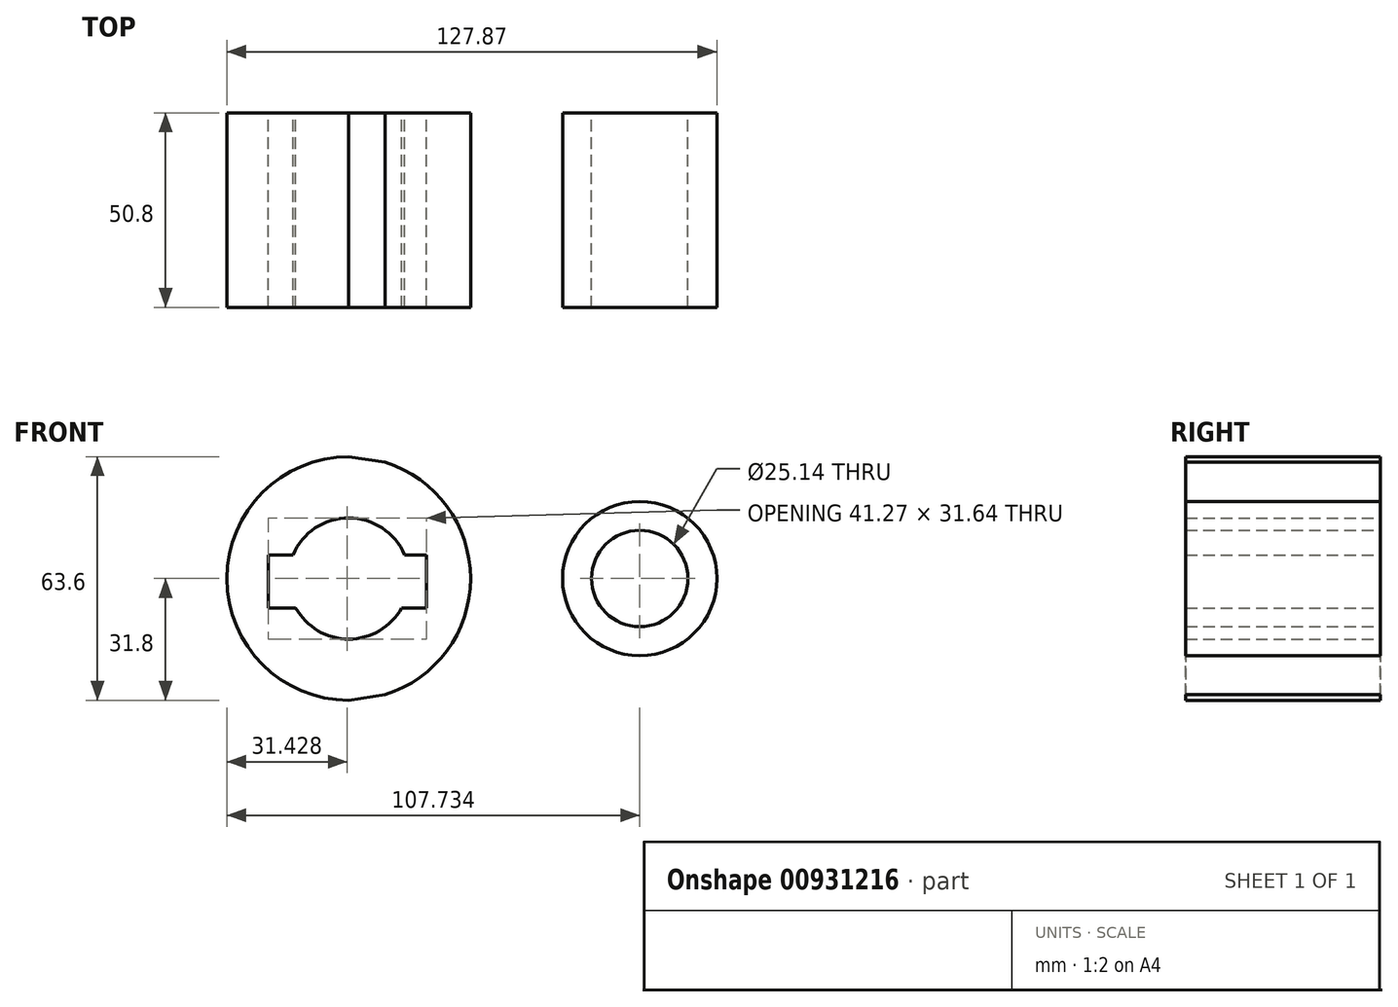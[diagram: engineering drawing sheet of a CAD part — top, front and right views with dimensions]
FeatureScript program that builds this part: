
annotation { "Feature Type Name" : "Feature", "Feature Type Description" : "" }
export const myFeature = defineFeature(function(context is Context, id is Id, definition is map)
    precondition{}
    {
        {
            var Q0;
            Q0=qCreatedBy(makeId("Front.planeOp"),FACE);
            var sketch = newSketch(context, id + "F0", { "sketchPlane" : qUnion([Q0])});
            skCircle(sketch, "E0", {"center": v(0, 0) * mm, "radius": 31.8 * mm});
            skCircle(sketch, "E1", {"center": v(75.93, 0) * mm, "radius": 20.13 * mm});
            skLineSegment(sketch, "E2", {"start": v(0, 31.8) * mm, "end": v(76.33, 20.13) * mm});
            skLineSegment(sketch, "E3", {"start": v(0, -31.8) * mm, "end": v(76.68, -20.12) * mm});
            skCircle(sketch, "E4", {"center": v(0, 0) * mm, "radius": 15.82 * mm});
            skCircle(sketch, "E5", {"center": v(75.93, 0) * mm, "radius": 12.57 * mm});
            skLineSegment(sketch, "E6.bottom", {"start": v(-21, 6.16) * mm, "end": v(20.27, 6.16) * mm});
            skLineSegment(sketch, "E6.top", {"start": v(-21, -7.68) * mm, "end": v(20.27, -7.68) * mm});
            skLineSegment(sketch, "E6.left", {"start": v(-21, 6.16) * mm, "end": v(-21, -7.68) * mm});
            skLineSegment(sketch, "E6.right", {"start": v(20.27, 6.16) * mm, "end": v(20.27, -7.68) * mm});
            skSolve(sketch);
        }
        {
            var Q0;
            Q0=makeQuery(id+"F0.imprint","IMPRINT",FACE,{"disambiguationData":[TD([[makeQuery(id+"F0.imprint","IMPRINT",EDGE,{"derivedFrom":sQuery(id+"F0.wireOp",EDGE,"E4")}),-1.0]])]});
            var Q1;
            {var subQ0=sQuery(id+"F0.wireOp",EDGE,"E2");var subQ1=sQuery(id+"F0.wireOp",EDGE,"E0");var subQ2=makeQuery(id+"F0.imprint","INTERSECT",VERTEX,{"disambiguationData":[OD(1.0)],"derivedFrom":[subQ1,subQ0]});Q1=makeQuery(id+"F0.imprint","IMPRINT",FACE,{"disambiguationData":[TD([[makeQuery(id+"F0.imprint","IMPRINT",EDGE,{"disambiguationData":[TD([[subQ2,1.0]])],"derivedFrom":subQ1}),-1.0]])]});}
            var Q2;
            Q2=makeQuery(id+"F0.imprint","IMPRINT",FACE,{"disambiguationData":[TD([[makeQuery(id+"F0.imprint","IMPRINT",EDGE,{"derivedFrom":sQuery(id+"F0.wireOp",EDGE,"E5")}),-1.0]])]});
            extrude(context, id + "F1", {"entities" : qUnion([Q0, Q1, Q2]), "depth" : 50.8 * mm, "offsetDistance" : 25.4 * mm});
        }
    });
